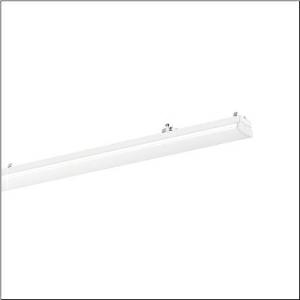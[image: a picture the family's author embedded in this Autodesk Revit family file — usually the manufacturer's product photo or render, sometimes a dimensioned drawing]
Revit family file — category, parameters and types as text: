
# Revit family: licross_11_recessed_opal_ho_51te1dcn4cxm
name_source: partatom
category: Lighting Fixtures
units: mm (PartAtom-declared; Revit-internal decimal feet)

## family parameters
Cut with Voids When Loaded = No
Host = Face
Light Source = No
Part Type = Normal
Room Calculation Point = No
Round Connector Dimension = Use Diameter
Shared = No

## types (1)
- --- (1 x LED, 12370 lm, 66.5 W, 4000K)
    Apparent Load = 67 VA
    CIE Flux Codes = 44 73 91 87 100
    Color Rendering = 80
    Color Temperature = 4000K
    Default Elevation = 1800 mm
    Description = Licross 11 recessed opal HO, luminaire insert, of sheet steel, coil coated, white, length: 1.500mm, width: 76mm, height: 87mm, LED rated luminous flux: 12.370lm, light colour: 840, SDCM (Standard Deviation of Colour Matching)MacAdam ≤ 2 SDCM (initial), control gear: ON/OFF Multilumen, CLOi, with plug, 3-pole, with phase selection, mains connection: 220..240V, AC, 50/60Hz, start of lifetime: 67W, end of service life: 75W, internal wiring halogen-free, primary optical cover: cover, of PMMA, light emission: direct with ceiling illumination distribution, primary light characteristic: symmetric, protection rating (complete): IP54, insulation class (complete): insulation class I (protective earthing), certification: CE, ENEC, VDE, UKCA, protection symbol: D if used in an environment with non-conductive dust loads with corresponding accessories, impact resistance: IK06, permissible ambient temperature for indoor applications: -35..+35°C, corresponds to IFS (International Featured Standards) requirements for safety and quality in the food industry, reducing of maximum allowable ambient temperature of 5°C with ceiling mounting, LABS conformity tested according to VDMA 24364:2018-05, The light source and the operating device comply with the requirements of the Ecodesign Regulation (EU) 2019/2020 and are replaceable in accordance with this regulation, packaging unit: 1 piece
    Height = 83 mm
    Lamp = 1 x LED
    Lamp Light Flux = 12370 lm
    Lamp Power = 66.5 W
    Lamp count = 1
    Length = 1500 mm
    Luminous efficacy = 186 lm/W
    Manufacturer = Siteco
    ModVariant = No
    Model = 51TE1DCN4CXM
    Mounting Place = Ceiling
    Mounting Type = Pendant
    Number of Poles = 1
    OnlyDefault = Yes
    Power Factor = 1
    Product Name = Licross 11 recessed opal HO
    Product group = luminaire insert | ceiling pendant
    ProductGroupID = 901
    Protection Class = Protection class I
    Protection Degree = IP 54
    RLX_Detail_Level = 1
    RLX_Emergency_Light_Flux = 0 lm
    RLX_Emergency_Type = 0
    RLX_Emergency_Type_DB = No
    RlxData = <blob elided: 24845 chars, md5=5a8da972>
    Socket = socket
    Standby Power = 0 W
    System Light Flux = 12370 lm
    System Power = 67 W
    Type Comments = factory setting: luminous flux: 100 % | (A | C | E) | 156 mA
    Type Image = l_1313666.jpg
    URL = http://relux.com
    VarID = @adj_000161
    Voltage = 0 V
    Weight = 0.00 kg
    Width = 76 mm

## geometry (parser evidence)
native form markers: Blend x4, Sweep x13
no freeform markers — native parametric forms only
